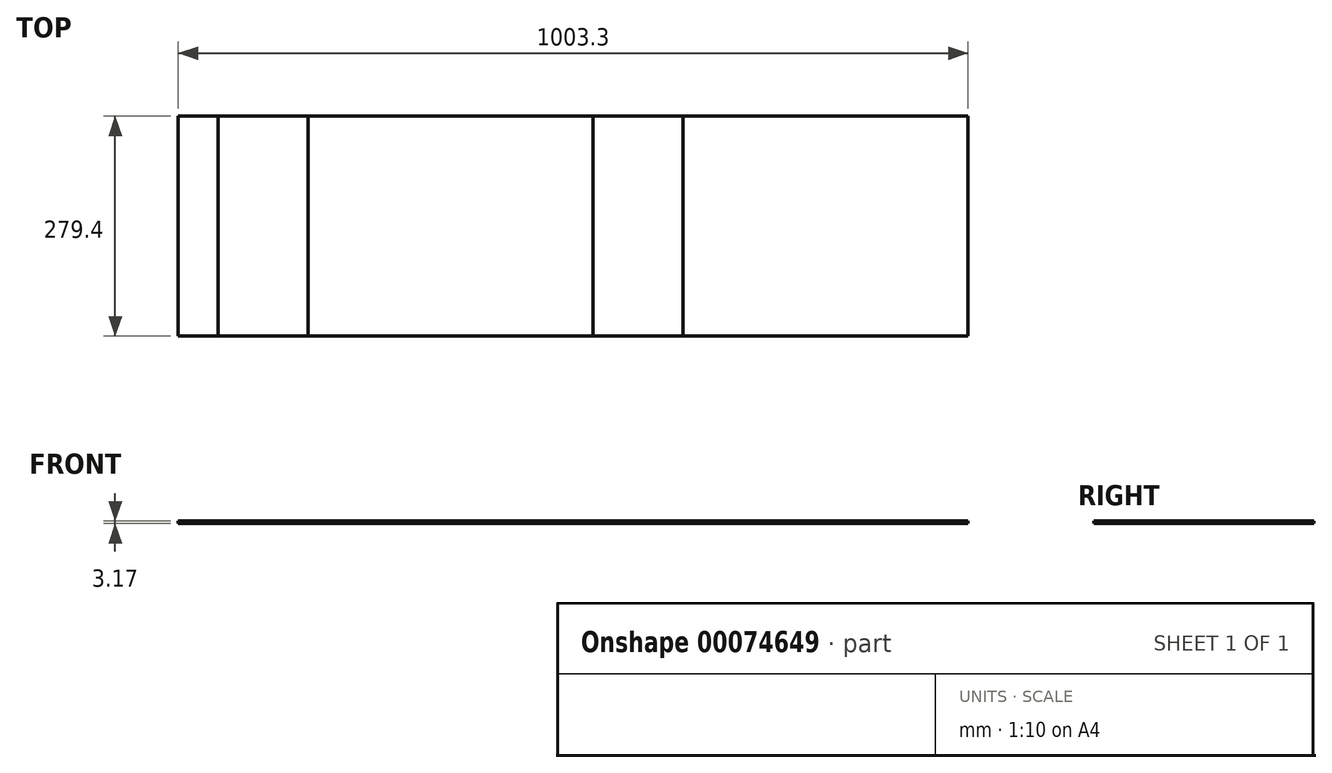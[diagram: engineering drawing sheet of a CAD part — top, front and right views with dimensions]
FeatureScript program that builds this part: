
annotation { "Feature Type Name" : "Feature", "Feature Type Description" : "" }
export const myFeature = defineFeature(function(context is Context, id is Id, definition is map)
    precondition{}
    {
        {
            var Q0;
            Q0=qCreatedBy(makeId("Top.planeOp"),FACE);
            var sketch = newSketch(context, id + "F0", { "sketchPlane" : qUnion([Q0])});
            skLineSegment(sketch, "E0.rect.bottom", {"start": v(-180.98, 139.7) * mm, "end": v(180.97, 139.7) * mm});
            skLineSegment(sketch, "E0.rect.top", {"start": v(-180.97, -139.7) * mm, "end": v(180.97, -139.7) * mm});
            skLineSegment(sketch, "E0.rect.left", {"start": v(-180.97, 139.7) * mm, "end": v(-180.97, -139.7) * mm});
            skLineSegment(sketch, "E0.rect.right", {"start": v(180.97, 139.7) * mm, "end": v(180.97, -139.7) * mm});
            skPoint(sketch, "E0.rect.middle", {"position": v(0, 0) * mm});
            skLineSegment(sketch, "E1.bottom", {"start": v(-180.98, 139.7) * mm, "end": v(-295.27, 139.7) * mm});
            skLineSegment(sketch, "E1.top", {"start": v(-180.97, -139.7) * mm, "end": v(-295.27, -139.7) * mm});
            skLineSegment(sketch, "E1.left", {"start": v(-180.98, 139.7) * mm, "end": v(-180.97, -139.7) * mm});
            skLineSegment(sketch, "E1.right", {"start": v(-295.27, 139.7) * mm, "end": v(-295.27, -139.7) * mm});
            skLineSegment(sketch, "E2.bottom", {"start": v(180.97, 139.7) * mm, "end": v(295.28, 139.7) * mm});
            skLineSegment(sketch, "E2.top", {"start": v(180.97, -139.7) * mm, "end": v(295.28, -139.7) * mm});
            skLineSegment(sketch, "E2.right", {"start": v(295.28, 139.7) * mm, "end": v(295.28, -139.7) * mm});
            skLineSegment(sketch, "E3.bottom", {"start": v(295.28, 139.7) * mm, "end": v(657.23, 139.7) * mm});
            skLineSegment(sketch, "E3.top", {"start": v(295.28, -139.7) * mm, "end": v(657.23, -139.7) * mm});
            skLineSegment(sketch, "E3.right", {"start": v(657.23, 139.7) * mm, "end": v(657.23, -139.7) * mm});
            skLineSegment(sketch, "E4.bottom", {"start": v(-295.27, -139.7) * mm, "end": v(-346.08, -139.7) * mm});
            skLineSegment(sketch, "E4.top", {"start": v(-295.27, 139.7) * mm, "end": v(-346.08, 139.7) * mm});
            skLineSegment(sketch, "E4.left", {"start": v(-295.27, -139.7) * mm, "end": v(-295.27, 139.7) * mm});
            skLineSegment(sketch, "E4.right", {"start": v(-346.08, -139.7) * mm, "end": v(-346.08, 139.7) * mm});
            skSolve(sketch);
        }
        {
            var Q0;
            Q0=makeQuery(id+"F0.imprint","IMPRINT",FACE,{"disambiguationData":[TD([[makeQuery(id+"F0.imprint","IMPRINT",EDGE,{"derivedFrom":sQuery(id+"F0.wireOp",EDGE,"E0.rect.bottom")}),-1.0]])]});
            extrude(context, id + "F1", {"entities" : qUnion([Q0]), "depth" : 3.17 * mm});
        }
        {
            var Q0;
            Q0=makeQuery(id+"F0.imprint","IMPRINT",FACE,{"disambiguationData":[TD([[makeQuery(id+"F0.imprint","IMPRINT",EDGE,{"derivedFrom":sQuery(id+"F0.wireOp",EDGE,"E1.bottom")}),1.0]])]});
            extrude(context, id + "F2", {"entities" : qUnion([Q0]), "depth" : 3.17 * mm});
        }
        {
            var Q0;
            Q0=makeQuery(id+"F0.imprint","IMPRINT",FACE,{"disambiguationData":[TD([[makeQuery(id+"F0.imprint","IMPRINT",EDGE,{"derivedFrom":sQuery(id+"F0.wireOp",EDGE,"E2.bottom")}),-1.0]])]});
            extrude(context, id + "F3", {"entities" : qUnion([Q0]), "depth" : 3.17 * mm});
        }
        {
            var Q0;
            Q0=makeQuery(id+"F0.imprint","IMPRINT",FACE,{"disambiguationData":[TD([[makeQuery(id+"F0.imprint","IMPRINT",EDGE,{"derivedFrom":sQuery(id+"F0.wireOp",EDGE,"E3.bottom")}),-1.0]])]});
            extrude(context, id + "F4", {"entities" : qUnion([Q0]), "depth" : 3.17 * mm});
        }
        {
            var Q0;
            Q0=makeQuery(id+"F0.imprint","IMPRINT",FACE,{"disambiguationData":[TD([[makeQuery(id+"F0.imprint","IMPRINT",EDGE,{"derivedFrom":sQuery(id+"F0.wireOp",EDGE,"E4.bottom")}),-1.0]])]});
            extrude(context, id + "F5", {"entities" : qUnion([Q0]), "depth" : 3.17 * mm});
        }
    });
